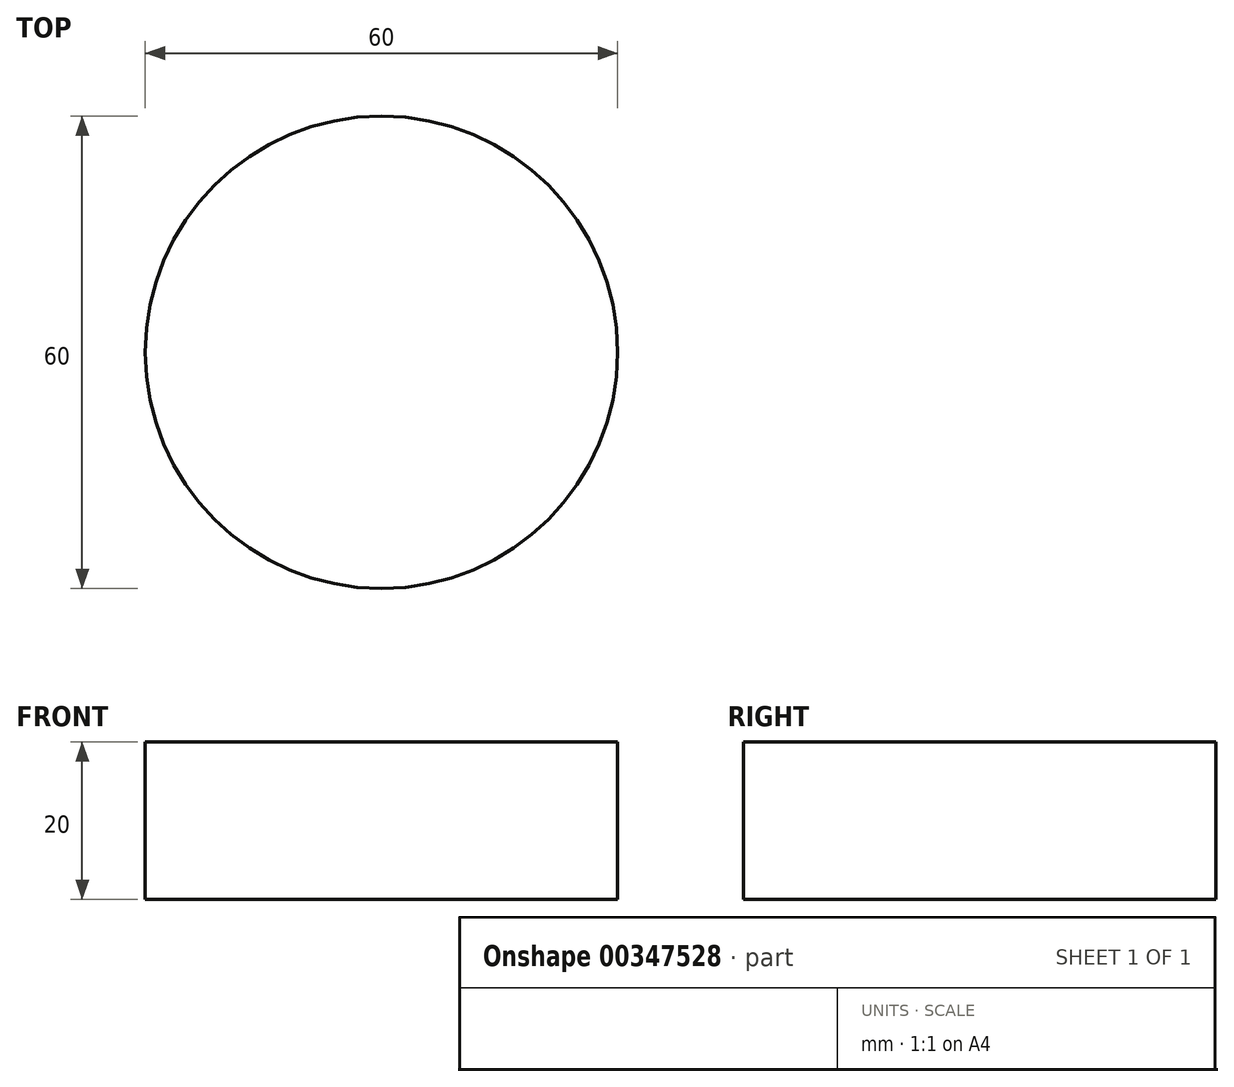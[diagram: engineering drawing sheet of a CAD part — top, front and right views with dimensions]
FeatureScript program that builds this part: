
annotation { "Feature Type Name" : "Feature", "Feature Type Description" : "" }
export const myFeature = defineFeature(function(context is Context, id is Id, definition is map)
    precondition{}
    {
        {
            var Q0;
            Q0=qCreatedBy(makeId("Top.planeOp"),FACE);
            var sketch = newSketch(context, id + "F0", { "sketchPlane" : qUnion([Q0])});
            skCircle(sketch, "E0", {"center": v(-41.55, 16.9) * mm, "radius": 30 * mm});
            skSolve(sketch);
        }
        {
            var Q0;
            Q0 = qSketchRegion(id + "F0", true);
            extrude(context, id + "F1", {"entities" : qUnion([Q0]), "depth" : 20 * mm});
        }
    });
